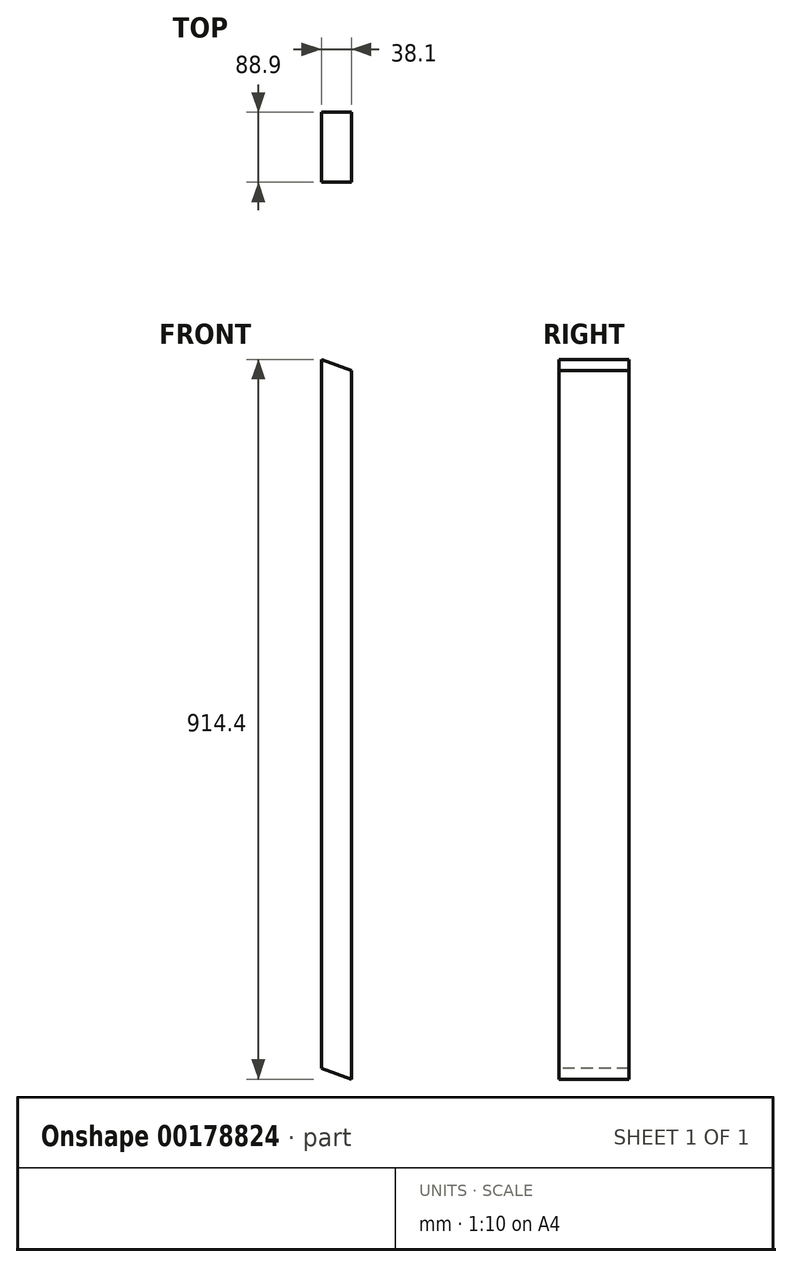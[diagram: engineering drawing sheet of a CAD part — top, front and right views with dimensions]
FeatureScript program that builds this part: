
annotation { "Feature Type Name" : "Feature", "Feature Type Description" : "" }
export const myFeature = defineFeature(function(context is Context, id is Id, definition is map)
    precondition{}
    {
        {
            var Q0;
            Q0=qCreatedBy(makeId("Front.planeOp"),FACE);
            var sketch = newSketch(context, id + "F0", { "sketchPlane" : qUnion([Q0])});
            skLineSegment(sketch, "E0.bottom", {"start": v(-38.1, 914.4) * mm, "end": v(0, 914.4) * mm});
            skLineSegment(sketch, "E0.top", {"start": v(-38.1, 0) * mm, "end": v(0, 0) * mm});
            skLineSegment(sketch, "E0.left", {"start": v(-38.1, 914.4) * mm, "end": v(-38.1, 0) * mm});
            skLineSegment(sketch, "E0.right", {"start": v(0, 914.4) * mm, "end": v(0, 0) * mm});
            skSolve(sketch);
        }
        {
            var Q0;
            Q0=makeQuery(id+"F0.imprint","IMPRINT",FACE,{"disambiguationData":[TD([[makeQuery(id+"F0.imprint","IMPRINT",EDGE,{"derivedFrom":sQuery(id+"F0.wireOp",EDGE,"E0.bottom")}),-1.0]])]});
            extrude(context, id + "F1", {"entities" : qUnion([Q0]), "depth" : 88.9 * mm});
        }
        {
            var Q0;
            Q0=makeQuery(id+"F1.opExtrude","CAP_FACE",FACE,{"disambiguationData":[OSD([sQuery(id+"F0.wireOp",EDGE,"E0.bottom"),sQuery(id+"F0.wireOp",EDGE,"E0.top"),sQuery(id+"F0.wireOp",EDGE,"E0.left"),sQuery(id+"F0.wireOp",EDGE,"E0.right")])],"isStart":false});
            var sketch = newSketch(context, id + "F2", { "sketchPlane" : qUnion([Q0])});
            skLineSegment(sketch, "E1", {"start": v(-38.1, 914.4) * mm, "end": v(0, 900.53) * mm});
            skLineSegment(sketch, "E2", {"start": v(0, 900.53) * mm, "end": v(0, 914.4) * mm});
            skLineSegment(sketch, "E3", {"start": v(0, 914.4) * mm, "end": v(-38.1, 914.4) * mm});
            skSolve(sketch);
        }
        {
            var Q0;
            Q0 = qSketchRegion(id + "F2", true);
            extrude(context, id + "F3", {"entities" : qUnion([Q0]), "operationType" : NewBodyOperationType.REMOVE, "oppositeDirection" : true, "depth" : 88.9 * mm});
        }
        {
            var Q0;
            Q0=makeQuery(id+"F1.opExtrude","CAP_FACE",FACE,{"disambiguationData":[OSD([sQuery(id+"F0.wireOp",EDGE,"E0.bottom"),sQuery(id+"F0.wireOp",EDGE,"E0.top"),sQuery(id+"F0.wireOp",EDGE,"E0.left"),sQuery(id+"F0.wireOp",EDGE,"E0.right")])],"isStart":false});
            var sketch = newSketch(context, id + "F4", { "sketchPlane" : qUnion([Q0])});
            skLineSegment(sketch, "E4", {"start": v(0, 0) * mm, "end": v(-38.1, 0) * mm});
            skLineSegment(sketch, "E5", {"start": v(-38.1, 0) * mm, "end": v(-38.1, 13.87) * mm});
            skLineSegment(sketch, "E6", {"start": v(-38.1, 13.87) * mm, "end": v(0, 0) * mm});
            skSolve(sketch);
        }
        {
            var Q0;
            Q0=makeQuery(id+"F4.imprint","IMPRINT",FACE,{"disambiguationData":[TD([[makeQuery(id+"F4.imprint","IMPRINT",EDGE,{"derivedFrom":sQuery(id+"F4.wireOp",EDGE,"E4")}),1.0]])]});
            extrude(context, id + "F5", {"entities" : qUnion([Q0]), "operationType" : NewBodyOperationType.REMOVE, "oppositeDirection" : true, "depth" : 88.9 * mm});
        }
    });
